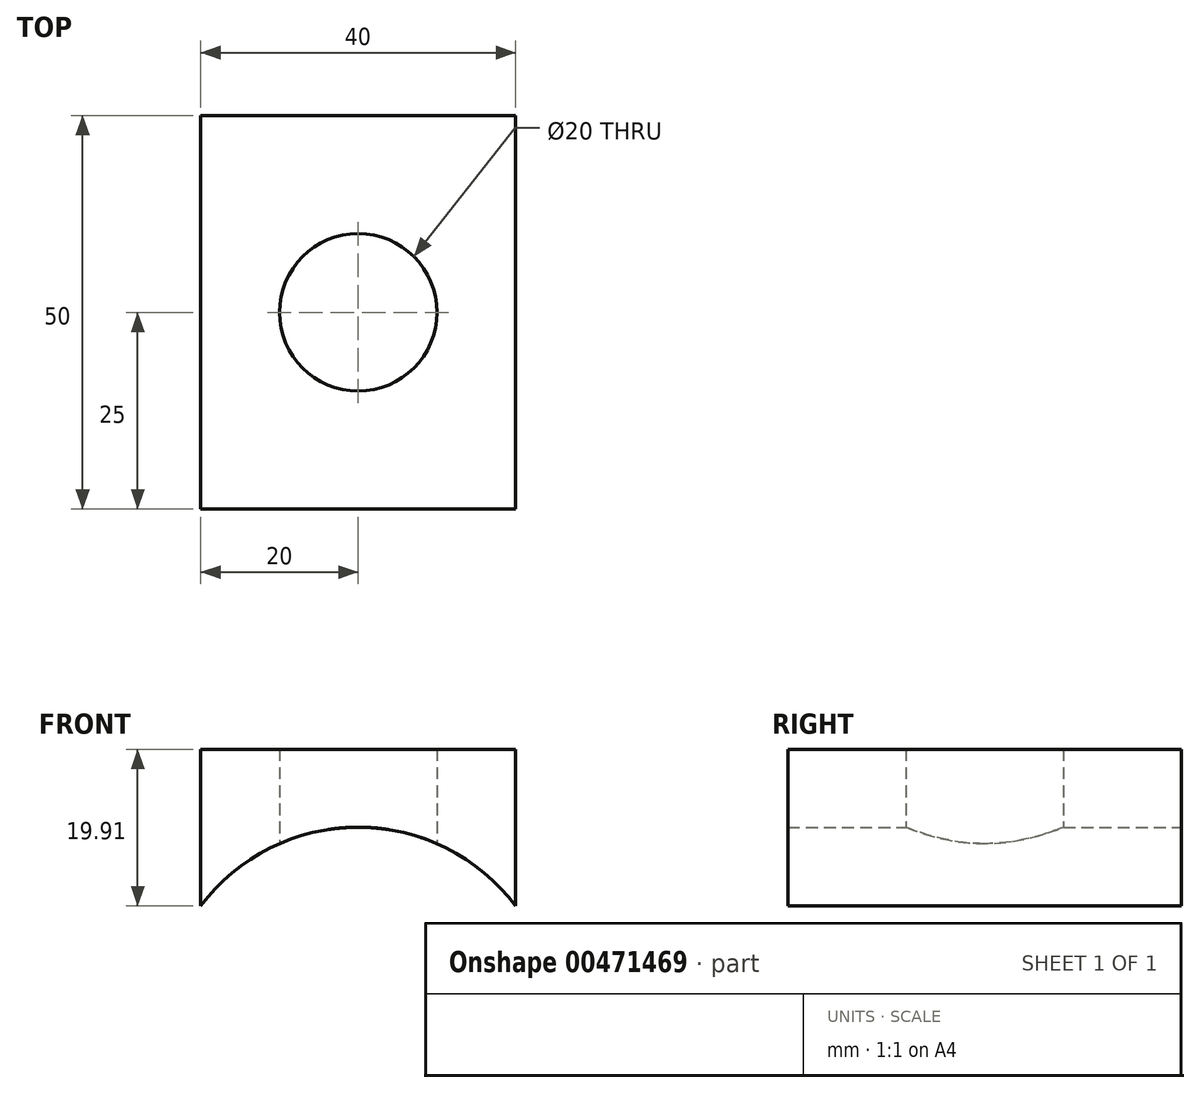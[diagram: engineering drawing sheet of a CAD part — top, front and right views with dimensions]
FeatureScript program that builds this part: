
annotation { "Feature Type Name" : "Feature", "Feature Type Description" : "" }
export const myFeature = defineFeature(function(context is Context, id is Id, definition is map)
    precondition{}
    {
        {
            var Q0;
            Q0=qCreatedBy(makeId("Front.planeOp"),FACE);
            var sketch = newSketch(context, id + "F0", { "sketchPlane" : qUnion([Q0])});
            skLineSegment(sketch, "E0.bottom", {"start": v(-20, 19.91) * mm, "end": v(20, 19.91) * mm});
            skLineSegment(sketch, "E0.top", {"start": v(-20, -0.09) * mm, "end": v(20, -0.09) * mm});
            skLineSegment(sketch, "E0.left", {"start": v(-20, 19.91) * mm, "end": v(-20, -0.09) * mm});
            skLineSegment(sketch, "E0.right", {"start": v(20, 19.91) * mm, "end": v(20, -0.09) * mm});
            skSolve(sketch);
        }
        {
            var Q0;
            Q0 = qSketchRegion(id + "F0", true);
            extrude(context, id + "F1", {"entities" : qUnion([Q0]), "depth" : 50 * mm});
        }
        {
            var Q0;
            Q0=qCreatedBy(makeId("Front.planeOp"),FACE);
            var sketch = newSketch(context, id + "F2", { "sketchPlane" : qUnion([Q0])});
            skCircle(sketch, "E1", {"center": v(0, -15) * mm, "radius": 25 * mm});
            skPoint(sketch, "E1.first.point", {"position": v(20, 0) * mm});
            skPoint(sketch, "E1.second.point", {"position": v(0, 10) * mm});
            skPoint(sketch, "E1.third.point", {"position": v(-20, 0) * mm});
            skSolve(sketch);
        }
        {
            var Q0;
            Q0 = qSketchRegion(id + "F2", true);
            extrude(context, id + "F3", {"entities" : qUnion([Q0]), "operationType" : NewBodyOperationType.REMOVE, "endBound" : BoundingType.THROUGH_ALL, "depth" : 25 * mm});
        }
        {
            var Q0;
            Q0=qCreatedBy(makeId("Top.planeOp"),FACE);
            var sketch = newSketch(context, id + "F4", { "sketchPlane" : qUnion([Q0])});
            skCircle(sketch, "E2", {"center": v(0, -25) * mm, "radius": 10 * mm});
            skSolve(sketch);
        }
        {
            var Q0;
            Q0 = qSketchRegion(id + "F4", true);
            extrude(context, id + "F5", {"entities" : qUnion([Q0]), "operationType" : NewBodyOperationType.REMOVE, "endBound" : BoundingType.THROUGH_ALL, "depth" : 25 * mm});
        }
    });
